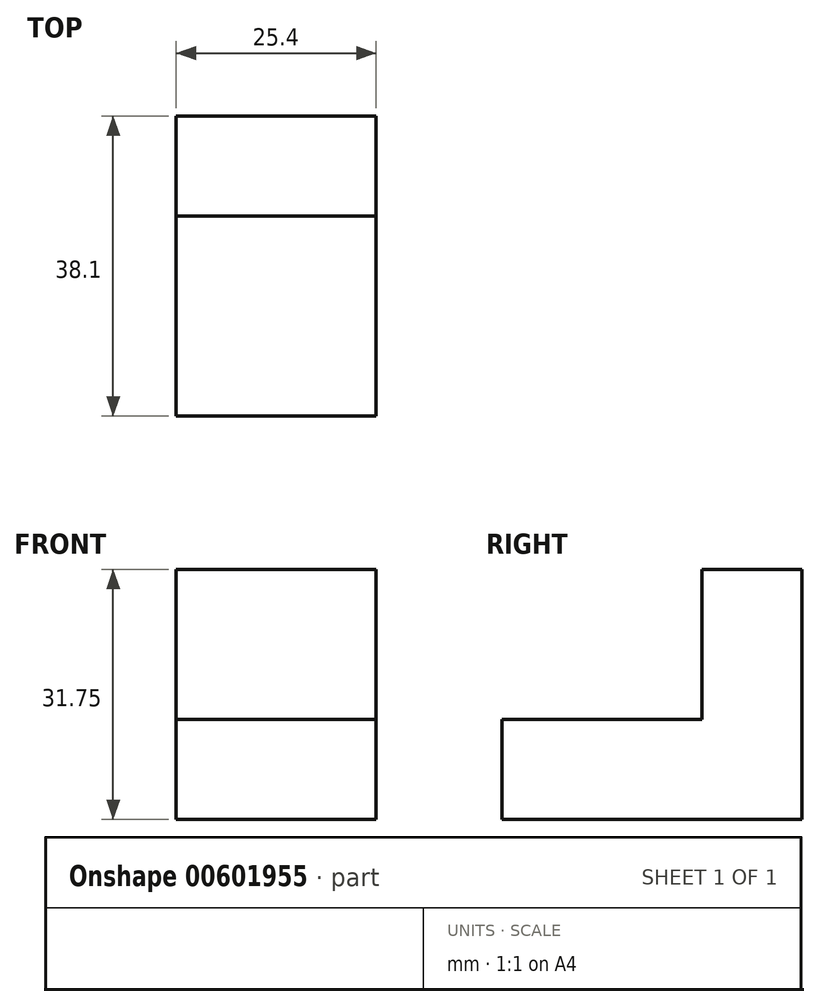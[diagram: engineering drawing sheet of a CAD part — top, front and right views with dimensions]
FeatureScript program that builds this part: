
annotation { "Feature Type Name" : "Feature", "Feature Type Description" : "" }
export const myFeature = defineFeature(function(context is Context, id is Id, definition is map)
    precondition{}
    {
        {
            var Q0;
            Q0=qCreatedBy(makeId("Right.planeOp"),FACE);
            var sketch = newSketch(context, id + "F0", { "sketchPlane" : qUnion([Q0])});
            skLineSegment(sketch, "E0", {"start": v(0, 0) * mm, "end": v(0, -31.75) * mm});
            skLineSegment(sketch, "E1", {"start": v(0, -31.75) * mm, "end": v(-38.1, -31.75) * mm});
            skLineSegment(sketch, "E2", {"start": v(-38.1, -31.75) * mm, "end": v(-38.1, -19.05) * mm});
            skLineSegment(sketch, "E3", {"start": v(-38.1, -19.05) * mm, "end": v(-12.7, -19.05) * mm});
            skLineSegment(sketch, "E4", {"start": v(-12.7, -19.05) * mm, "end": v(-12.7, 0) * mm});
            skLineSegment(sketch, "E5", {"start": v(-12.7, 0) * mm, "end": v(0, 0) * mm});
            skSolve(sketch);
        }
        {
            var Q0;
            Q0=makeQuery(id+"F0.imprint","IMPRINT",FACE,{"disambiguationData":[TD([[makeQuery(id+"F0.imprint","IMPRINT",EDGE,{"derivedFrom":sQuery(id+"F0.wireOp",EDGE,"E0")}),-1.0]])]});
            extrude(context, id + "F1", {"entities" : qUnion([Q0]), "depth" : 25.4 * mm, "offsetDistance" : 25.4 * mm});
        }
    });
